# Revit family: Accessory-Towel_Bar-KOHLER-ELLISTON-K-72784T
name_source: partatom
category: Specialty Equipment
revit_build: Autodesk Revit 2017 (Build: 20160225_1515(x64)
units: mm (PartAtom-declared; Revit-internal decimal feet)

## family parameters
Cut with Voids When Loaded = No
Host = Face
OmniClass Number = 23.31.25.25
OmniClass Title = Towel Bars
Part Type = Normal
Room Calculation Point = No
Round Connector Dimension = Use Diameter
Shared = No

## types (2) — shared parameters
ADA Compliant = No
Assembly Code = C1030200
Date Modified = 07/15/2020
Default Elevation = 42"
Description = 18 INCH TOWEL BAR OL
Height = 2"
Length = 3 3/8"
Manufacturer = KOHLER Co.
Master Format 2014 = 10 28 00
Master Format 2014 Name = Toilet, Bath, and Laundry Accessories
Material = Premium Metal Constraction
Product Name = ELLISTON
URL = http://www.kohler.com.cn
WaterSense Certified = No
Width = 18"

## per-type parameters (varying)
| type | Finish | Model | Type |
| CP-Polished Chrome | Kohler-Metal-CP-Polished_Chrome | K-72784T-CP | 1 |
| BN-Roman Silver | Kohler-Metal-BN-Vibrant_Brushed_Nickel | K-72784T-BN | 2 |

## geometry (parser evidence)
native form markers: Sweep x3
no freeform markers — native parametric forms only
